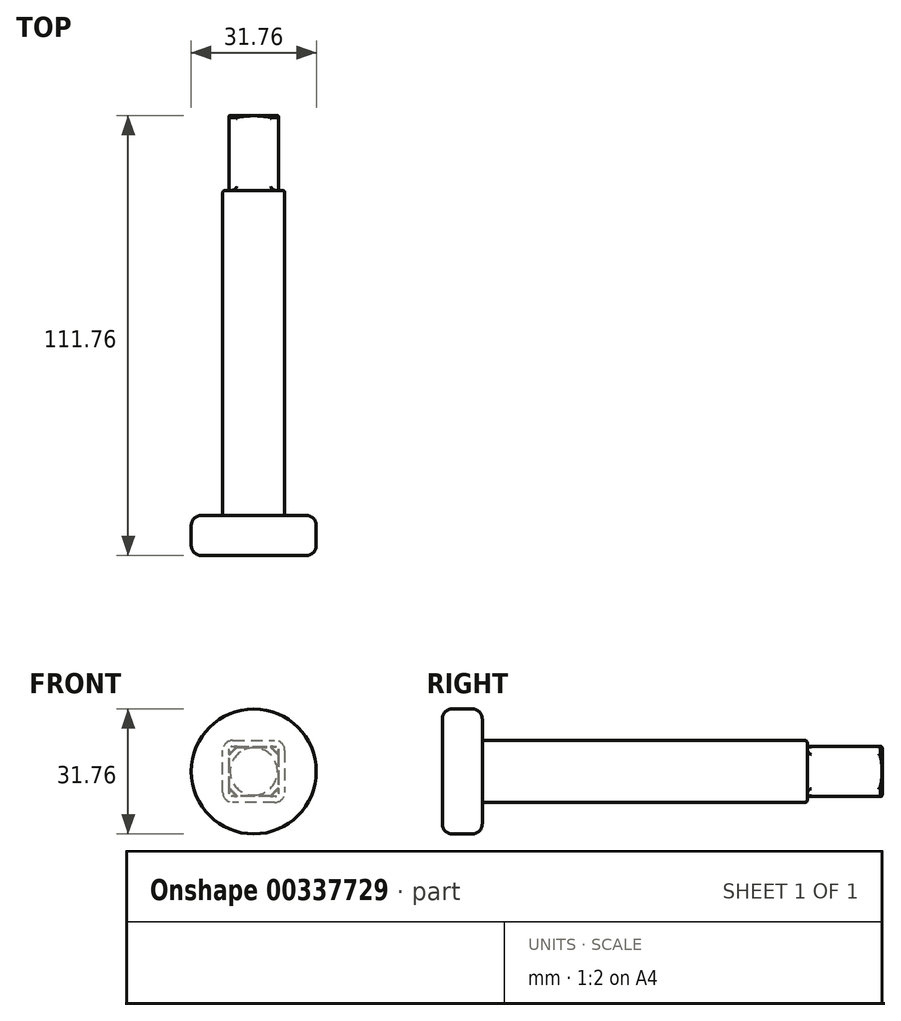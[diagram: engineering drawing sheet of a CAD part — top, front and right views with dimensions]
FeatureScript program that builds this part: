
annotation { "Feature Type Name" : "Feature", "Feature Type Description" : "" }
export const myFeature = defineFeature(function(context is Context, id is Id, definition is map)
    precondition{}
    {
        {
            var Q0;
            Q0=qCreatedBy(makeId("Front.planeOp"),FACE);
            var sketch = newSketch(context, id + "F0", { "sketchPlane" : qUnion([Q0])});
            skCircle(sketch, "E0.cCircle", {"center": v(0, 0) * mm, "radius": 7.87 * mm, "construction": true});
            skLineSegment(sketch, "E0.0", {"start": v(7.87, -7.87) * mm, "end": v(-7.87, -7.87) * mm});
            skLineSegment(sketch, "E0.1", {"start": v(-7.87, -7.87) * mm, "end": v(-7.87, 7.87) * mm});
            skLineSegment(sketch, "E0.2", {"start": v(-7.87, 7.87) * mm, "end": v(7.87, 7.87) * mm});
            skLineSegment(sketch, "E0.3", {"start": v(7.87, 7.87) * mm, "end": v(7.87, -7.87) * mm});
            skPoint(sketch, "E0.0.midPoint", {"position": v(0, -7.87) * mm});
            skSolve(sketch);
        }
        {
            var Q0;
            Q0=makeQuery(id+"F0.imprint","IMPRINT",FACE,{"disambiguationData":[TD([[makeQuery(id+"F0.imprint","IMPRINT",EDGE,{"derivedFrom":sQuery(id+"F0.wireOp",EDGE,"E0.0")}),-1.0]])]});
            extrude(context, id + "F1", {"entities" : qUnion([Q0]), "depth" : 82.55 * mm});
        }
        {
            var Q0;
            Q0=qCreatedBy(makeId("Front.planeOp"),FACE);
            var sketch = newSketch(context, id + "F2", { "sketchPlane" : qUnion([Q0])});
            skCircle(sketch, "E1.cCircle", {"center": v(0, 0) * mm, "radius": 6.34 * mm, "construction": true});
            skLineSegment(sketch, "E1.0", {"start": v(-6.34, 6.34) * mm, "end": v(6.34, 6.34) * mm});
            skLineSegment(sketch, "E1.1", {"start": v(6.34, 6.34) * mm, "end": v(6.34, -6.34) * mm});
            skLineSegment(sketch, "E1.2", {"start": v(6.34, -6.34) * mm, "end": v(-6.34, -6.34) * mm});
            skLineSegment(sketch, "E1.3", {"start": v(-6.34, -6.34) * mm, "end": v(-6.34, 6.34) * mm});
            skPoint(sketch, "E1.0.midPoint", {"position": v(0, 6.34) * mm});
            skSolve(sketch);
        }
        {
            var Q0;
            Q0=makeQuery(id+"F2.imprint","IMPRINT",FACE,{"disambiguationData":[TD([[makeQuery(id+"F2.imprint","IMPRINT",EDGE,{"derivedFrom":sQuery(id+"F2.wireOp",EDGE,"E1.0")}),-1.0]])]});
            extrude(context, id + "F3", {"entities" : qUnion([Q0]), "operationType" : NewBodyOperationType.ADD, "depth" : -19.05 * mm});
        }
        {
            var Q0;
            Q0=makeQuery(id+"F1.opExtrude","CAP_FACE",FACE,{"disambiguationData":[OSD([sQuery(id+"F0.wireOp",EDGE,"E0.0"),sQuery(id+"F0.wireOp",EDGE,"E0.1"),sQuery(id+"F0.wireOp",EDGE,"E0.2"),sQuery(id+"F0.wireOp",EDGE,"E0.3")])],"isStart":false});
            var sketch = newSketch(context, id + "F4", { "sketchPlane" : qUnion([Q0])});
            skCircle(sketch, "E2", {"center": v(0, 0) * mm, "radius": 15.88 * mm});
            skSolve(sketch);
        }
        {
            var Q0;
            Q0=makeQuery(id+"F4.imprint","IMPRINT",FACE,{"disambiguationData":[TD([[makeQuery(id+"F4.imprint","IMPRINT",EDGE,{"derivedFrom":sQuery(id+"F4.wireOp",EDGE,"E2")}),1.0]])]});
            var Q1;
            Q1=makeQuery(id+"F4.imprint","IMPRINT",FACE,{"disambiguationData":[TD([[makeQuery(id+"F4.imprint","IMPRINT",EDGE,{"derivedFrom":makeQuery(id+"F1.opExtrude","CAP_EDGE",EDGE,{"disambiguationData":[OSD([sQuery(id+"F0.wireOp",EDGE,"E0.0")])],"isStart":false})}),-1.0]])]});
            extrude(context, id + "F5", {"entities" : qUnion([Q0, Q1]), "operationType" : NewBodyOperationType.ADD, "depth" : 10.16 * mm});
        }
        {
            var Q0;
            Q0=makeQuery(id+"F5.opExtrude","CAP_EDGE",EDGE,{"disambiguationData":[OSD([sQuery(id+"F4.wireOp",EDGE,"E2")])],"isStart":false});
            var Q1;
            Q1=makeQuery(id+"F5.opExtrude","CAP_EDGE",EDGE,{"disambiguationData":[OSD([sQuery(id+"F4.wireOp",EDGE,"E2")])],"isStart":true});
            var Q2;
            Q2=makeQuery(id+"F1.opExtrude","CAP_EDGE",EDGE,{"disambiguationData":[OSD([sQuery(id+"F0.wireOp",EDGE,"E0.0")])],"isStart":false});
            var Q3;
            Q3=makeQuery(id+"F1.opExtrude","CAP_EDGE",EDGE,{"disambiguationData":[OSD([sQuery(id+"F0.wireOp",EDGE,"E0.1")])],"isStart":false});
            fillet(context, id + "F6", {"entities" : qUnion([Q0, Q1, Q2, Q3]), "radius" : 2.54 * mm, "tangentPropagation" : true, "allowEdgeOverflow" : false});
        }
        {
            var Q0;
            Q0=makeQuery(id+"F1.opExtrude","SWEPT_EDGE",EDGE,{"disambiguationData":[OSD([sQuery(id+"F0.wireOp",EDGE,"E0.0"),sQuery(id+"F0.wireOp",EDGE,"E0.1")])]});
            var Q1;
            Q1=makeQuery(id+"F1.opExtrude","SWEPT_EDGE",EDGE,{"disambiguationData":[OSD([sQuery(id+"F0.wireOp",EDGE,"E0.0"),sQuery(id+"F0.wireOp",EDGE,"E0.3")])]});
            var Q2;
            Q2=makeQuery(id+"F1.opExtrude","SWEPT_EDGE",EDGE,{"disambiguationData":[OSD([sQuery(id+"F0.wireOp",EDGE,"E0.2"),sQuery(id+"F0.wireOp",EDGE,"E0.3")])]});
            var Q3;
            Q3=makeQuery(id+"F1.opExtrude","SWEPT_EDGE",EDGE,{"disambiguationData":[OSD([sQuery(id+"F0.wireOp",EDGE,"E0.1"),sQuery(id+"F0.wireOp",EDGE,"E0.2")])]});
            var Q4;
            Q4=makeQuery(id+"F1.opExtrude","CAP_EDGE",EDGE,{"disambiguationData":[OSD([sQuery(id+"F0.wireOp",EDGE,"E0.2")])],"isStart":false});
            var Q5;
            Q5=makeQuery(id+"F5.opExtrude","CAP_EDGE",EDGE,{"disambiguationData":[OSD([sQuery(id+"F4.wireOp",EDGE,"E2")])],"isStart":true});
            var Q6;
            Q6=makeQuery(id+"F5.opExtrude","CAP_EDGE",EDGE,{"disambiguationData":[OSD([sQuery(id+"F4.wireOp",EDGE,"E2")])],"isStart":false});
            fillet(context, id + "F7", {"entities" : qUnion([Q0, Q1, Q2, Q3, Q4, Q5, Q6]), "radius" : 2.54 * mm, "tangentPropagation" : true, "allowEdgeOverflow" : false});
        }
        {
            var Q0;
            Q0=makeQuery(id+"F3.opExtrude","SWEPT_EDGE",EDGE,{"disambiguationData":[OSD([sQuery(id+"F2.wireOp",EDGE,"E1.0"),sQuery(id+"F2.wireOp",EDGE,"E1.1")])]});
            var Q1;
            Q1=makeQuery(id+"F3.opExtrude","SWEPT_EDGE",EDGE,{"disambiguationData":[OSD([sQuery(id+"F2.wireOp",EDGE,"E1.1"),sQuery(id+"F2.wireOp",EDGE,"E1.2")])]});
            var Q2;
            Q2=makeQuery(id+"F3.opExtrude","SWEPT_EDGE",EDGE,{"disambiguationData":[OSD([sQuery(id+"F2.wireOp",EDGE,"E1.0"),sQuery(id+"F2.wireOp",EDGE,"E1.3")])]});
            var Q3;
            Q3=makeQuery(id+"F3.opExtrude","SWEPT_EDGE",EDGE,{"disambiguationData":[OSD([sQuery(id+"F2.wireOp",EDGE,"E1.2"),sQuery(id+"F2.wireOp",EDGE,"E1.3")])]});
            chamfer(context, id + "F8", {"entities" : qUnion([Q0, Q1, Q2, Q3]), "width" : 2.03 * mm, "tangentPropagation" : true});
        }
        {
            var Q0;
            Q0=qCreatedBy(makeId("Right.planeOp"),FACE);
            var sketch = newSketch(context, id + "F9", { "sketchPlane" : qUnion([Q0])});
            skLineSegment(sketch, "E3", {"start": v(0, 0) * mm, "end": v(21.59, 0) * mm});
            skArc(sketch, "E4", {"start": v(19.98, 0) * mm, "mid": v(19.09, 5.9) * mm, "end": v(16.5, 11.27) * mm});
            skLineSegment(sketch, "E5", {"start": v(21.59, 11.27) * mm, "end": v(16.5, 11.27) * mm});
            skLineSegment(sketch, "E6", {"start": v(21.59, 11.27) * mm, "end": v(21.59, 0) * mm});
            skSolve(sketch);
        }
        {
            var Q0;
            {var subQ2=sQuery(id+"F9.wireOp",EDGE,"E4");Q0=makeQuery(id+"F9.imprint","IMPRINT",FACE,{"disambiguationData":[TD([[makeQuery(id+"F9.imprint","IMPRINT",EDGE,{"derivedFrom":subQ2}),-1.0]])]});}
            var Q1;
            Q1=sQuery(id+"F9.wireOp",EDGE,"E3");
            revolve(context, id + "F10", {"operationType" : NewBodyOperationType.REMOVE, "entities" : qUnion([Q0]), "axis" : qUnion([Q1]), "revolveType" : RevolveType.FULL, "oppositeDirection" : true});
        }
        {
            var Q0;
            Q0=makeQuery(id+"F3.opExtrude","CAP_EDGE",EDGE,{"disambiguationData":[OSD([sQuery(id+"F2.wireOp",EDGE,"E1.3")])],"isStart":true});
            var Q1;
            Q1=makeQuery(id+"F8.opChamfer","BLEND_EDGE",EDGE,{"blendedFrom":[makeQuery(id+"F3.opExtrude","SWEPT_EDGE",EDGE,{"disambiguationData":[OSD([sQuery(id+"F2.wireOp",EDGE,"E1.2"),sQuery(id+"F2.wireOp",EDGE,"E1.3")])]}),makeQuery(id+"F1.opExtrude","CAP_FACE",FACE,{"disambiguationData":[OSD([sQuery(id+"F0.wireOp",EDGE,"E0.0"),sQuery(id+"F0.wireOp",EDGE,"E0.1"),sQuery(id+"F0.wireOp",EDGE,"E0.2"),sQuery(id+"F0.wireOp",EDGE,"E0.3")])],"isStart":true})],"blendedInto":[makeQuery(id+"F1.opExtrude","CAP_FACE",FACE,{"disambiguationData":[OSD([sQuery(id+"F0.wireOp",EDGE,"E0.0"),sQuery(id+"F0.wireOp",EDGE,"E0.1"),sQuery(id+"F0.wireOp",EDGE,"E0.2"),sQuery(id+"F0.wireOp",EDGE,"E0.3")])],"isStart":true})]});
            var Q2;
            Q2=makeQuery(id+"F3.opExtrude","CAP_EDGE",EDGE,{"disambiguationData":[OSD([sQuery(id+"F2.wireOp",EDGE,"E1.2")])],"isStart":true});
            var Q3;
            Q3=makeQuery(id+"F8.opChamfer","BLEND_EDGE",EDGE,{"blendedFrom":[makeQuery(id+"F3.opExtrude","SWEPT_EDGE",EDGE,{"disambiguationData":[OSD([sQuery(id+"F2.wireOp",EDGE,"E1.0"),sQuery(id+"F2.wireOp",EDGE,"E1.3")])]}),makeQuery(id+"F1.opExtrude","CAP_FACE",FACE,{"disambiguationData":[OSD([sQuery(id+"F0.wireOp",EDGE,"E0.0"),sQuery(id+"F0.wireOp",EDGE,"E0.1"),sQuery(id+"F0.wireOp",EDGE,"E0.2"),sQuery(id+"F0.wireOp",EDGE,"E0.3")])],"isStart":true})],"blendedInto":[makeQuery(id+"F1.opExtrude","CAP_FACE",FACE,{"disambiguationData":[OSD([sQuery(id+"F0.wireOp",EDGE,"E0.0"),sQuery(id+"F0.wireOp",EDGE,"E0.1"),sQuery(id+"F0.wireOp",EDGE,"E0.2"),sQuery(id+"F0.wireOp",EDGE,"E0.3")])],"isStart":true})]});
            var Q4;
            Q4=makeQuery(id+"F3.opExtrude","CAP_EDGE",EDGE,{"disambiguationData":[OSD([sQuery(id+"F2.wireOp",EDGE,"E1.0")])],"isStart":true});
            var Q5;
            Q5=makeQuery(id+"F8.opChamfer","BLEND_EDGE",EDGE,{"blendedFrom":[makeQuery(id+"F3.opExtrude","SWEPT_EDGE",EDGE,{"disambiguationData":[OSD([sQuery(id+"F2.wireOp",EDGE,"E1.0"),sQuery(id+"F2.wireOp",EDGE,"E1.1")])]}),makeQuery(id+"F1.opExtrude","CAP_FACE",FACE,{"disambiguationData":[OSD([sQuery(id+"F0.wireOp",EDGE,"E0.0"),sQuery(id+"F0.wireOp",EDGE,"E0.1"),sQuery(id+"F0.wireOp",EDGE,"E0.2"),sQuery(id+"F0.wireOp",EDGE,"E0.3")])],"isStart":true})],"blendedInto":[makeQuery(id+"F1.opExtrude","CAP_FACE",FACE,{"disambiguationData":[OSD([sQuery(id+"F0.wireOp",EDGE,"E0.0"),sQuery(id+"F0.wireOp",EDGE,"E0.1"),sQuery(id+"F0.wireOp",EDGE,"E0.2"),sQuery(id+"F0.wireOp",EDGE,"E0.3")])],"isStart":true})]});
            var Q6;
            Q6=makeQuery(id+"F3.opExtrude","CAP_EDGE",EDGE,{"disambiguationData":[OSD([sQuery(id+"F2.wireOp",EDGE,"E1.1")])],"isStart":true});
            var Q7;
            Q7=makeQuery(id+"F8.opChamfer","BLEND_EDGE",EDGE,{"blendedFrom":[makeQuery(id+"F3.opExtrude","SWEPT_EDGE",EDGE,{"disambiguationData":[OSD([sQuery(id+"F2.wireOp",EDGE,"E1.1"),sQuery(id+"F2.wireOp",EDGE,"E1.2")])]}),makeQuery(id+"F1.opExtrude","CAP_FACE",FACE,{"disambiguationData":[OSD([sQuery(id+"F0.wireOp",EDGE,"E0.0"),sQuery(id+"F0.wireOp",EDGE,"E0.1"),sQuery(id+"F0.wireOp",EDGE,"E0.2"),sQuery(id+"F0.wireOp",EDGE,"E0.3")])],"isStart":true})],"blendedInto":[makeQuery(id+"F1.opExtrude","CAP_FACE",FACE,{"disambiguationData":[OSD([sQuery(id+"F0.wireOp",EDGE,"E0.0"),sQuery(id+"F0.wireOp",EDGE,"E0.1"),sQuery(id+"F0.wireOp",EDGE,"E0.2"),sQuery(id+"F0.wireOp",EDGE,"E0.3")])],"isStart":true})]});
            fillet(context, id + "F11", {"entities" : qUnion([Q0, Q1, Q2, Q3, Q4, Q5, Q6, Q7]), "radius" : 1.02 * mm, "tangentPropagation" : true, "allowEdgeOverflow" : false});
        }
        {
            var Q0;
            Q0=makeQuery(id+"F1.opExtrude","CAP_EDGE",EDGE,{"disambiguationData":[OSD([sQuery(id+"F0.wireOp",EDGE,"E0.2")])],"isStart":true});
            fillet(context, id + "F12", {"entities" : qUnion([Q0]), "radius" : 0.5 * mm, "tangentPropagation" : true, "allowEdgeOverflow" : false});
        }
        {
            var Q0;
            {var subQ0=sQuery(id+"F2.wireOp",EDGE,"E1.2");Q0=makeQuery(id+"F8.opChamfer","BLEND_EDGE",EDGE,{"blendedFrom":[makeQuery(id+"F3.opExtrude","SWEPT_EDGE",EDGE,{"disambiguationData":[OSD([sQuery(id+"F2.wireOp",EDGE,"E1.1"),subQ0])]}),makeQuery(id+"F3.opExtrude","SWEPT_FACE",FACE,{"disambiguationData":[OSD([subQ0])]})],"blendedInto":[makeQuery(id+"F3.opExtrude","SWEPT_FACE",FACE,{"disambiguationData":[OSD([subQ0])]})]});}
            var Q1;
            {var subQ0=sQuery(id+"F2.wireOp",EDGE,"E1.1");Q1=makeQuery(id+"F8.opChamfer","BLEND_EDGE",EDGE,{"blendedFrom":[makeQuery(id+"F3.opExtrude","SWEPT_EDGE",EDGE,{"disambiguationData":[OSD([subQ0,sQuery(id+"F2.wireOp",EDGE,"E1.2")])]}),makeQuery(id+"F3.opExtrude","SWEPT_FACE",FACE,{"disambiguationData":[OSD([subQ0])]})],"blendedInto":[makeQuery(id+"F3.opExtrude","SWEPT_FACE",FACE,{"disambiguationData":[OSD([subQ0])]})]});}
            var Q2;
            {var subQ0=sQuery(id+"F2.wireOp",EDGE,"E1.2");Q2=makeQuery(id+"F8.opChamfer","BLEND_EDGE",EDGE,{"blendedFrom":[makeQuery(id+"F3.opExtrude","SWEPT_EDGE",EDGE,{"disambiguationData":[OSD([subQ0,sQuery(id+"F2.wireOp",EDGE,"E1.3")])]}),makeQuery(id+"F3.opExtrude","SWEPT_FACE",FACE,{"disambiguationData":[OSD([subQ0])]})],"blendedInto":[makeQuery(id+"F3.opExtrude","SWEPT_FACE",FACE,{"disambiguationData":[OSD([subQ0])]})]});}
            var Q3;
            {var subQ0=sQuery(id+"F2.wireOp",EDGE,"E1.3");Q3=makeQuery(id+"F8.opChamfer","BLEND_EDGE",EDGE,{"blendedFrom":[makeQuery(id+"F3.opExtrude","SWEPT_EDGE",EDGE,{"disambiguationData":[OSD([sQuery(id+"F2.wireOp",EDGE,"E1.2"),subQ0])]}),makeQuery(id+"F3.opExtrude","SWEPT_FACE",FACE,{"disambiguationData":[OSD([subQ0])]})],"blendedInto":[makeQuery(id+"F3.opExtrude","SWEPT_FACE",FACE,{"disambiguationData":[OSD([subQ0])]})]});}
            var Q4;
            {var subQ0=sQuery(id+"F2.wireOp",EDGE,"E1.3");Q4=makeQuery(id+"F8.opChamfer","BLEND_EDGE",EDGE,{"blendedFrom":[makeQuery(id+"F3.opExtrude","SWEPT_EDGE",EDGE,{"disambiguationData":[OSD([sQuery(id+"F2.wireOp",EDGE,"E1.0"),subQ0])]}),makeQuery(id+"F3.opExtrude","SWEPT_FACE",FACE,{"disambiguationData":[OSD([subQ0])]})],"blendedInto":[makeQuery(id+"F3.opExtrude","SWEPT_FACE",FACE,{"disambiguationData":[OSD([subQ0])]})]});}
            var Q5;
            {var subQ0=sQuery(id+"F2.wireOp",EDGE,"E1.0");Q5=makeQuery(id+"F8.opChamfer","BLEND_EDGE",EDGE,{"blendedFrom":[makeQuery(id+"F3.opExtrude","SWEPT_EDGE",EDGE,{"disambiguationData":[OSD([subQ0,sQuery(id+"F2.wireOp",EDGE,"E1.3")])]}),makeQuery(id+"F3.opExtrude","SWEPT_FACE",FACE,{"disambiguationData":[OSD([subQ0])]})],"blendedInto":[makeQuery(id+"F3.opExtrude","SWEPT_FACE",FACE,{"disambiguationData":[OSD([subQ0])]})]});}
            var Q6;
            {var subQ0=sQuery(id+"F2.wireOp",EDGE,"E1.0");Q6=makeQuery(id+"F8.opChamfer","BLEND_EDGE",EDGE,{"blendedFrom":[makeQuery(id+"F3.opExtrude","SWEPT_EDGE",EDGE,{"disambiguationData":[OSD([subQ0,sQuery(id+"F2.wireOp",EDGE,"E1.1")])]}),makeQuery(id+"F3.opExtrude","SWEPT_FACE",FACE,{"disambiguationData":[OSD([subQ0])]})],"blendedInto":[makeQuery(id+"F3.opExtrude","SWEPT_FACE",FACE,{"disambiguationData":[OSD([subQ0])]})]});}
            var Q7;
            {var subQ0=sQuery(id+"F2.wireOp",EDGE,"E1.1");Q7=makeQuery(id+"F8.opChamfer","BLEND_EDGE",EDGE,{"blendedFrom":[makeQuery(id+"F3.opExtrude","SWEPT_EDGE",EDGE,{"disambiguationData":[OSD([sQuery(id+"F2.wireOp",EDGE,"E1.0"),subQ0])]}),makeQuery(id+"F3.opExtrude","SWEPT_FACE",FACE,{"disambiguationData":[OSD([subQ0])]})],"blendedInto":[makeQuery(id+"F3.opExtrude","SWEPT_FACE",FACE,{"disambiguationData":[OSD([subQ0])]})]});}
            var Q8;
            Q8=makeQuery(id+"F10.boolean.opBoolean","INTERSECT",EDGE,{"derivedFrom":[makeQuery(id+"F3.opExtrude","SWEPT_FACE",FACE,{"disambiguationData":[OSD([sQuery(id+"F2.wireOp",EDGE,"E1.1")])]}),makeQuery(id+"F10.opRevolve","SWEPT_FACE",FACE,{"disambiguationData":[OSD([sQuery(id+"F9.wireOp",EDGE,"E4")])]})]});
            var Q9;
            Q9=makeQuery(id+"F10.boolean.opBoolean","INTERSECT",EDGE,{"derivedFrom":[makeQuery(id+"F8.opChamfer","BLEND_FACE",FACE,{"disambiguationData":[OSD([sQuery(id+"F2.wireOp",EDGE,"E1.0"),sQuery(id+"F2.wireOp",EDGE,"E1.1")])]}),makeQuery(id+"F10.opRevolve","SWEPT_FACE",FACE,{"disambiguationData":[OSD([sQuery(id+"F9.wireOp",EDGE,"E4")])]})]});
            var Q10;
            Q10=makeQuery(id+"F10.boolean.opBoolean","INTERSECT",EDGE,{"derivedFrom":[makeQuery(id+"F3.opExtrude","SWEPT_FACE",FACE,{"disambiguationData":[OSD([sQuery(id+"F2.wireOp",EDGE,"E1.0")])]}),makeQuery(id+"F10.opRevolve","SWEPT_FACE",FACE,{"disambiguationData":[OSD([sQuery(id+"F9.wireOp",EDGE,"E4")])]})]});
            var Q11;
            Q11=makeQuery(id+"F10.boolean.opBoolean","INTERSECT",EDGE,{"derivedFrom":[makeQuery(id+"F8.opChamfer","BLEND_FACE",FACE,{"disambiguationData":[OSD([sQuery(id+"F2.wireOp",EDGE,"E1.0"),sQuery(id+"F2.wireOp",EDGE,"E1.3")])]}),makeQuery(id+"F10.opRevolve","SWEPT_FACE",FACE,{"disambiguationData":[OSD([sQuery(id+"F9.wireOp",EDGE,"E4")])]})]});
            var Q12;
            Q12=makeQuery(id+"F10.boolean.opBoolean","INTERSECT",EDGE,{"derivedFrom":[makeQuery(id+"F3.opExtrude","SWEPT_FACE",FACE,{"disambiguationData":[OSD([sQuery(id+"F2.wireOp",EDGE,"E1.3")])]}),makeQuery(id+"F10.opRevolve","SWEPT_FACE",FACE,{"disambiguationData":[OSD([sQuery(id+"F9.wireOp",EDGE,"E4")])]})]});
            var Q13;
            Q13=makeQuery(id+"F10.boolean.opBoolean","INTERSECT",EDGE,{"derivedFrom":[makeQuery(id+"F8.opChamfer","BLEND_FACE",FACE,{"disambiguationData":[OSD([sQuery(id+"F2.wireOp",EDGE,"E1.2"),sQuery(id+"F2.wireOp",EDGE,"E1.3")])]}),makeQuery(id+"F10.opRevolve","SWEPT_FACE",FACE,{"disambiguationData":[OSD([sQuery(id+"F9.wireOp",EDGE,"E4")])]})]});
            var Q14;
            Q14=makeQuery(id+"F10.boolean.opBoolean","INTERSECT",EDGE,{"derivedFrom":[makeQuery(id+"F3.opExtrude","SWEPT_FACE",FACE,{"disambiguationData":[OSD([sQuery(id+"F2.wireOp",EDGE,"E1.2")])]}),makeQuery(id+"F10.opRevolve","SWEPT_FACE",FACE,{"disambiguationData":[OSD([sQuery(id+"F9.wireOp",EDGE,"E4")])]})]});
            var Q15;
            Q15=makeQuery(id+"F10.boolean.opBoolean","INTERSECT",EDGE,{"derivedFrom":[makeQuery(id+"F8.opChamfer","BLEND_FACE",FACE,{"disambiguationData":[OSD([sQuery(id+"F2.wireOp",EDGE,"E1.1"),sQuery(id+"F2.wireOp",EDGE,"E1.2")])]}),makeQuery(id+"F10.opRevolve","SWEPT_FACE",FACE,{"disambiguationData":[OSD([sQuery(id+"F9.wireOp",EDGE,"E4")])]})]});
            fillet(context, id + "F13", {"entities" : qUnion([Q0, Q1, Q2, Q3, Q4, Q5, Q6, Q7, Q8, Q9, Q10, Q11, Q12, Q13, Q14, Q15]), "radius" : 0.25 * mm, "tangentPropagation" : true, "allowEdgeOverflow" : false});
        }
    });
